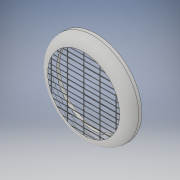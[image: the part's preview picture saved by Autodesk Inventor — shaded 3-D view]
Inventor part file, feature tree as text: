
AUTODESK INVENTOR PART (.ipt)
format: ipt  version: 2017 (Build 210142000, 142)  size: 144,896 bytes
history: native  units: in
note: dims shown in document units (in); Inventor stores cm internally (conversion verified against a paired STEP export)
features: extrude x1, fillet x1, shell x1, sketch x1
ambient origin geometry x8: Origin, YZ Plane, XZ Plane, XY Plane, X Axis, Y Axis, Z Axis, Center Point
bodies: Solid1 (feature_tree)
feature tree (4):
  extrude  "Extrusion1"  Depth=1.0in TaperAngle=0.0deg
  fillet  "Fillet1"  Radius=0.75in
  shell  "Shell1"  Thickness=0.7in
  sketch  "Sketch1"  dims[d0=7.1875in d1=1.0in d2=0.0in d3=0.75in d4=0.7in]
